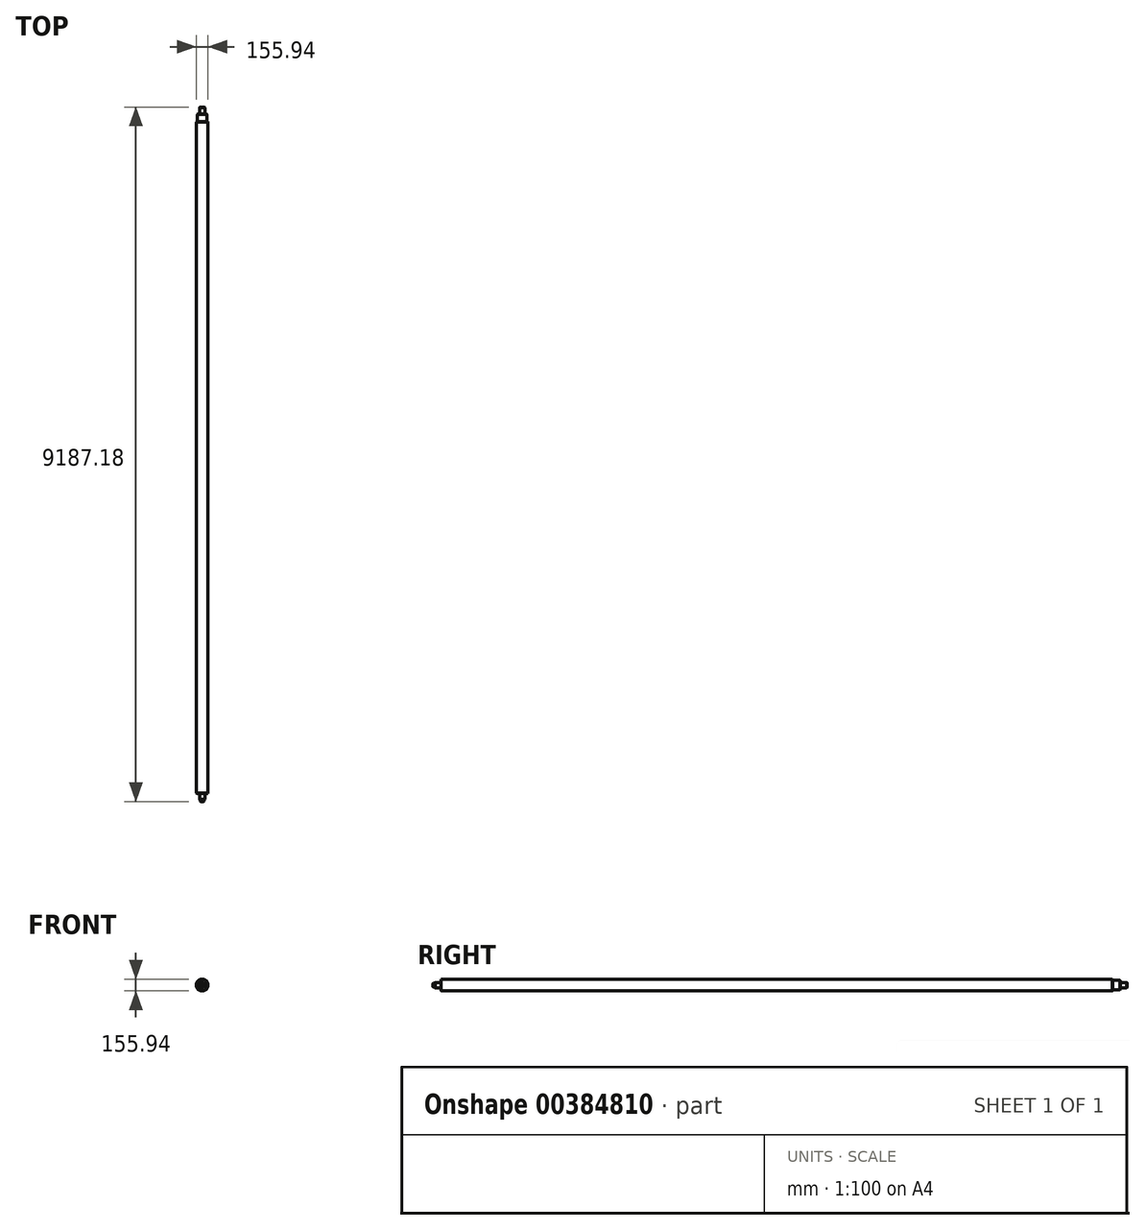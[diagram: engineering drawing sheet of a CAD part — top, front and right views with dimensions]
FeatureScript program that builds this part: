
annotation { "Feature Type Name" : "Feature", "Feature Type Description" : "" }
export const myFeature = defineFeature(function(context is Context, id is Id, definition is map)
    precondition{}
    {
        {
            var Q0;
            Q0=qCreatedBy(makeId("Front.planeOp"),FACE);
            var sketch = newSketch(context, id + "F0", { "sketchPlane" : qUnion([Q0])});
            skCircle(sketch, "E0", {"center": v(0, 0) * mm, "radius": 77.97 * mm});
            skSolve(sketch);
        }
        {
            var Q0;
            Q0 = qSketchRegion(id + "F0", true);
            extrude(context, id + "F1", {"entities" : qUnion([Q0]), "oppositeDirection" : true, "depth" : 8890 * mm});
        }
        {
            var Q0;
            Q0=makeQuery(id+"F1.opExtrude","CAP_FACE",FACE,{"disambiguationData":[OSD([sQuery(id+"F0.wireOp",EDGE,"E0")])],"isStart":true});
            var sketch = newSketch(context, id + "F2", { "sketchPlane" : qUnion([Q0])});
            skCircle(sketch, "E1", {"center": v(0, 0) * mm, "radius": 35.4 * mm});
            skSolve(sketch);
        }
        {
            var Q0;
            Q0 = qSketchRegion(id + "F2", true);
            extrude(context, id + "F3", {"entities" : qUnion([Q0]), "operationType" : NewBodyOperationType.ADD, "depth" : 81.28 * mm});
        }
        {
            var Q0;
            Q0=makeQuery(id+"F3.opExtrude","CAP_FACE",FACE,{"disambiguationData":[OSD([sQuery(id+"F2.wireOp",EDGE,"E1")])],"isStart":false});
            var sketch = newSketch(context, id + "F4", { "sketchPlane" : qUnion([Q0])});
            skCircle(sketch, "E2", {"center": v(0, 0) * mm, "radius": 23.99 * mm});
            skSolve(sketch);
        }
        {
            var Q0;
            Q0 = qSketchRegion(id + "F4", true);
            var Q1;
            Q1=makeQuery(id+"F1.opExtrude","CAP_FACE",FACE,{"disambiguationData":[OSD([sQuery(id+"F0.wireOp",EDGE,"E0")])],"isStart":false});
            extrude(context, id + "F5", {"entities" : qUnion([Q0, Q1]), "operationType" : NewBodyOperationType.ADD, "depth" : 25.4 * mm});
        }
        {
            var Q0;
            Q0=makeQuery(id+"F1.opExtrude","CAP_FACE",FACE,{"disambiguationData":[OSD([sQuery(id+"F0.wireOp",EDGE,"E0")])],"isStart":false});
            var sketch = newSketch(context, id + "F6", { "sketchPlane" : qUnion([Q0])});
            skCircle(sketch, "E3", {"center": v(0, 0) * mm, "radius": 62.05 * mm});
            skSolve(sketch);
        }
        {
            var Q0;
            Q0=makeQuery(id+"F6.imprint","IMPRINT",FACE,{"disambiguationData":[TD([[makeQuery(id+"F6.imprint","IMPRINT",EDGE,{"derivedFrom":sQuery(id+"F6.wireOp",EDGE,"E3")}),1.0]])]});
            extrude(context, id + "F7", {"entities" : qUnion([Q0]), "operationType" : NewBodyOperationType.ADD, "depth" : 101.6 * mm});
        }
        {
            var Q0;
            Q0=makeQuery(id+"F7.opExtrude","CAP_FACE",FACE,{"disambiguationData":[OSD([sQuery(id+"F6.wireOp",EDGE,"E3")])],"isStart":false});
            var sketch = newSketch(context, id + "F8", { "sketchPlane" : qUnion([Q0])});
            skCircle(sketch, "E4", {"center": v(0, 0) * mm, "radius": 34.4 * mm});
            skSolve(sketch);
        }
        {
            var Q0;
            Q0 = qSketchRegion(id + "F8", true);
            extrude(context, id + "F9", {"entities" : qUnion([Q0]), "operationType" : NewBodyOperationType.ADD, "depth" : 88.9 * mm});
        }
        {
            var Q0;
            Q0=makeQuery(id+"F9.opExtrude","CAP_EDGE",EDGE,{"disambiguationData":[OSD([sQuery(id+"F8.wireOp",EDGE,"E4")])],"isStart":false});
            var Q1;
            Q1=makeQuery(id+"F7.opExtrude","CAP_EDGE",EDGE,{"disambiguationData":[OSD([sQuery(id+"F6.wireOp",EDGE,"E3")])],"isStart":false});
            var Q2;
            Q2=makeQuery(id+"F1.opExtrude","CAP_EDGE",EDGE,{"disambiguationData":[OSD([sQuery(id+"F0.wireOp",EDGE,"E0")])],"isStart":false});
            var Q3;
            Q3=makeQuery(id+"F1.opExtrude","CAP_EDGE",EDGE,{"disambiguationData":[OSD([sQuery(id+"F0.wireOp",EDGE,"E0")])],"isStart":true});
            var Q4;
            Q4=makeQuery(id+"F3.opExtrude","CAP_EDGE",EDGE,{"disambiguationData":[OSD([sQuery(id+"F2.wireOp",EDGE,"E1")])],"isStart":false});
            var Q5;
            Q5=makeQuery(id+"F5.opExtrude","CAP_EDGE",EDGE,{"disambiguationData":[OSD([sQuery(id+"F4.wireOp",EDGE,"E2")])],"isStart":false});
            chamfer(context, id + "F10", {"entities" : qUnion([Q0, Q1, Q2, Q3, Q4, Q5]), "width" : 5.08 * mm, "tangentPropagation" : true});
        }
    });
